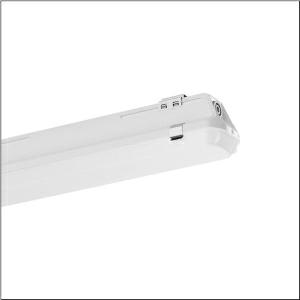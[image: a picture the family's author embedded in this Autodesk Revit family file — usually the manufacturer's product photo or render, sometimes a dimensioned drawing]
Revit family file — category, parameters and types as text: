
# Revit family: monsun_r__11_51fp108p430h_5d5d
name_source: partatom
category: Lighting Fixtures
units: mm (PartAtom-declared; Revit-internal decimal feet)

## family parameters
Cut with Voids When Loaded = No
Host = Face
Light Source = No
Part Type = Normal
Room Calculation Point = No
Round Connector Dimension = Use Diameter
Shared = No

## types (1)
- Monsun® 11 (1 x LED, 3970 lm, 22.2 W, 4000K)
    Apparent Load = 22 VA
    CIE Flux Codes = 47 77 93 94 100
    Color Rendering = 80
    Color Temperature = 4000K
    Default Elevation = 1800 mm
    Description = Monsun® 11, damp-proof luminaire, chain hanger, primary optical cover: enclosure, of PMMA, light emission: direct distribution, primary light characteristic: symmetric, installation type: suspended mounting, surface-mounted, horizontal mounting, vertical mounting, LED, rated luminous flux: 3.970lm, luminous efficacy: 179lm/W, light colour: 840, colour temperature: 4000K, control gear: ECG, with terminal, 3-pole, max. 2.5mm², mains connection: 220..240V, AC, 50/60Hz, rated input power: 22W, luminaire housing, of glass-fibre reinforced polyester, uncoated, bright grey, incl. chain hanger, length: 1.590mm, width: 90mm, height: 88mm, clip for enclosure, of stainless steel (V2A), ceiling mounting element, of stainless steel (V2A), chain hanger, of stainless steel (V2A), protection rating (complete): IP66, insulation class (complete): insulation class I (protective earthing), certification: CE, ENEC, VDE, UKCA, protection symbol: D, impact resistance: IK04, permissible operating ambient temperature: -35..+40°C, standard: EN 50419, EN 60598-2-1, no direct snow, no direct sun, no direct rain, for indoor or canopied outdoor use, corresponds to IFS (International Featured Standards) requirements for safety and quality in the food industry, contact your sales advisor before using the luminaires in applications with unclear chemical exposure, large temperature fluctuations or condensation-forming humidity, LABS conformity tested according to VDMA 24364:2018-05, packaging unit: 1 piece
    Height = 89 mm
    Lamp = 1 x LED
    Lamp Light Flux = 3970 lm
    Lamp Power = 22.2 W
    Lamp count = 1
    Length = 1590 mm
    Luminous efficacy = 179 lm/W
    Manufacturer = Siteco
    ModVariant = No
    Model = 51FP108P430H
    Mounting Place = Ceiling
    Mounting Type = Surface mounted
    Number of Poles = 1
    OnlyDefault = Yes
    Power Factor = 1
    Product Name = Monsun® 11
    Product group = damp-proof luminaire
    ProductGroupID = 301
    Protection Class = Protection class I
    Protection Degree = IP 66
    RLX_Detail_Level = 1
    RLX_Emergency_Light_Flux = 0 lm
    RLX_Emergency_Type = 0
    RLX_Emergency_Type_DB = No
    RlxData = <blob elided: 88273 chars, md5=478b2f2c>
    Socket = socket
    Standby Power = 0 W
    System Light Flux = 3970 lm
    System Power = 22 W
    Type Comments = Product without accessories
    Type Image = l_1004748.jpg
    URL = http://relux.com
    VarID = ---
    Voltage = 0 V
    Weight = 0.00 kg
    Width = 90 mm

## geometry (parser evidence)
native form markers: Blend x4, Sweep x15
no freeform markers — native parametric forms only
